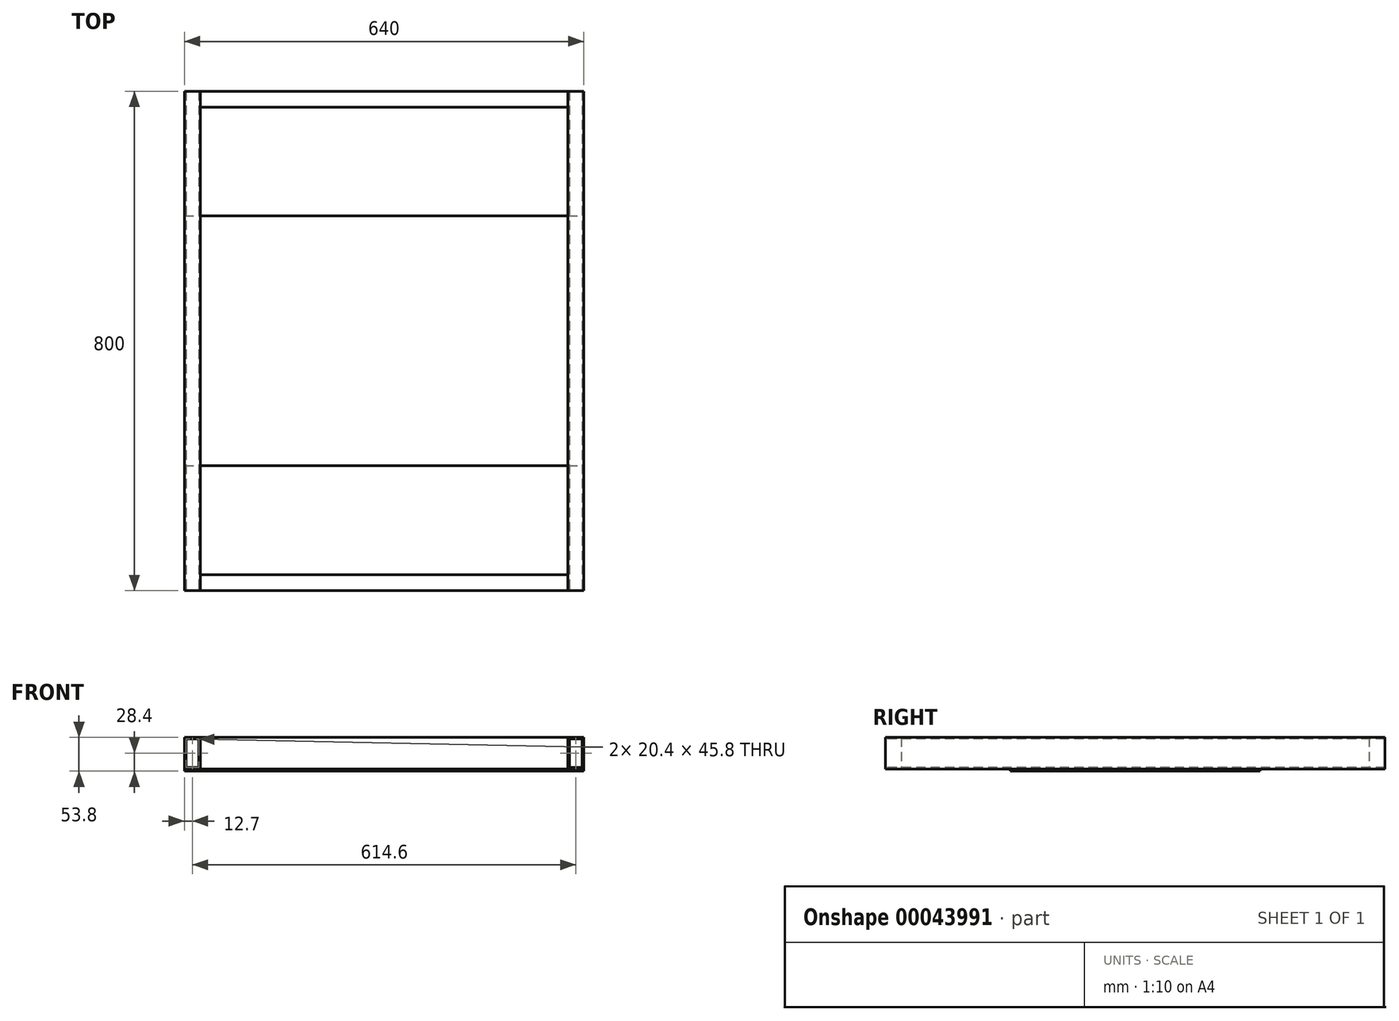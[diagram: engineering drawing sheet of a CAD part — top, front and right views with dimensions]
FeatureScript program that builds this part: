
annotation { "Feature Type Name" : "Feature", "Feature Type Description" : "" }
export const myFeature = defineFeature(function(context is Context, id is Id, definition is map)
    precondition{}
    {
        {
            var Q0;
            Q0=qCreatedBy(makeId("Top.planeOp"),FACE);
            var sketch = newSketch(context, id + "F0", { "sketchPlane" : qUnion([Q0])});
            skLineSegment(sketch, "E0", {"start": v(0, 0) * mm, "end": v(294.6, 0) * mm, "construction": true});
            skLineSegment(sketch, "E1", {"start": v(0, 0) * mm, "end": v(-294.6, 0) * mm, "construction": true});
            skLineSegment(sketch, "E2.bottom", {"start": v(-320, 400) * mm, "end": v(-294.6, 400) * mm});
            skLineSegment(sketch, "E2.top", {"start": v(-320, -400) * mm, "end": v(-294.6, -400) * mm});
            skLineSegment(sketch, "E2.left", {"start": v(-320, 400) * mm, "end": v(-320, -400) * mm});
            skLineSegment(sketch, "E2.right", {"start": v(-294.6, 400) * mm, "end": v(-294.6, -400) * mm});
            skLineSegment(sketch, "E3.bottom", {"start": v(294.6, 400) * mm, "end": v(320, 400) * mm});
            skLineSegment(sketch, "E3.top", {"start": v(294.6, -400) * mm, "end": v(320, -400) * mm});
            skLineSegment(sketch, "E3.left", {"start": v(294.6, 400) * mm, "end": v(294.6, -400) * mm});
            skLineSegment(sketch, "E3.right", {"start": v(320, 400) * mm, "end": v(320, -400) * mm});
            skLineSegment(sketch, "E4.bottom", {"start": v(-294.6, 400) * mm, "end": v(294.6, 400) * mm});
            skLineSegment(sketch, "E4.top", {"start": v(-294.6, 374.6) * mm, "end": v(294.6, 374.6) * mm});
            skLineSegment(sketch, "E4.left", {"start": v(-294.6, 400) * mm, "end": v(-294.6, 374.6) * mm});
            skLineSegment(sketch, "E4.right", {"start": v(294.6, 400) * mm, "end": v(294.6, 374.6) * mm});
            skLineSegment(sketch, "E5.bottom", {"start": v(-294.6, -400) * mm, "end": v(294.6, -400) * mm});
            skLineSegment(sketch, "E5.top", {"start": v(-294.6, -374.6) * mm, "end": v(294.6, -374.6) * mm});
            skLineSegment(sketch, "E5.left", {"start": v(-294.6, -400) * mm, "end": v(-294.6, -374.6) * mm});
            skLineSegment(sketch, "E5.right", {"start": v(294.6, -400) * mm, "end": v(294.6, -374.6) * mm});
            skSolve(sketch);
        }
        {
            var Q0;
            Q0=makeQuery(id+"F0.imprint","IMPRINT",FACE,{"disambiguationData":[TD([[makeQuery(id+"F0.imprint","IMPRINT",EDGE,{"derivedFrom":sQuery(id+"F0.wireOp",EDGE,"E2.bottom")}),-1.0]])]});
            extrude(context, id + "F1", {"entities" : qUnion([Q0]), "depth" : 50.8 * mm});
        }
        {
            var Q0;
            Q0=makeQuery(id+"F0.imprint","IMPRINT",FACE,{"disambiguationData":[TD([[makeQuery(id+"F0.imprint","IMPRINT",EDGE,{"derivedFrom":sQuery(id+"F0.wireOp",EDGE,"E4.bottom")}),-1.0]])]});
            extrude(context, id + "F2", {"entities" : qUnion([Q0]), "depth" : 50.8 * mm});
        }
        {
            var Q0;
            Q0=makeQuery(id+"F0.imprint","IMPRINT",FACE,{"disambiguationData":[TD([[makeQuery(id+"F0.imprint","IMPRINT",EDGE,{"derivedFrom":sQuery(id+"F0.wireOp",EDGE,"E3.bottom")}),-1.0]])]});
            extrude(context, id + "F3", {"entities" : qUnion([Q0]), "depth" : 50.8 * mm});
        }
        {
            var Q0;
            Q0=makeQuery(id+"F0.imprint","IMPRINT",FACE,{"disambiguationData":[TD([[makeQuery(id+"F0.imprint","IMPRINT",EDGE,{"derivedFrom":sQuery(id+"F0.wireOp",EDGE,"E5.bottom")}),1.0]])]});
            extrude(context, id + "F4", {"entities" : qUnion([Q0]), "depth" : 50.8 * mm});
        }
        {
            var Q0;
            Q0=makeQuery(id+"F0.imprint","IMPRINT",FACE,{"disambiguationData":[TD([[makeQuery(id+"F0.imprint","IMPRINT",EDGE,{"derivedFrom":sQuery(id+"F0.wireOp",EDGE,"E2.right")}),1.0]])]});
            var sketch = newSketch(context, id + "F5", { "sketchPlane" : qUnion([Q0])});
            skLineSegment(sketch, "E6.rect.bottom", {"start": v(-320, -200) * mm, "end": v(320, -200) * mm});
            skLineSegment(sketch, "E6.rect.top", {"start": v(-320, 200) * mm, "end": v(320, 200) * mm});
            skLineSegment(sketch, "E6.rect.left", {"start": v(-320, -200) * mm, "end": v(-320, 200) * mm});
            skLineSegment(sketch, "E6.rect.right", {"start": v(320, -200) * mm, "end": v(320, 200) * mm});
            skPoint(sketch, "E6.rect.middle", {"position": v(0, 0) * mm});
            skSolve(sketch);
        }
        {
            var Q0;
            Q0 = qSketchRegion(id + "F5", true);
            extrude(context, id + "F6", {"entities" : qUnion([Q0]), "oppositeDirection" : true, "depth" : 3 * mm});
        }
        {
            var Q0;
            Q0=makeQuery(id+"F1.opExtrude","SWEPT_FACE",FACE,{"disambiguationData":[OSD([sQuery(id+"F0.wireOp",EDGE,"E2.top")])]});
            var Q1;
            Q1=makeQuery(id+"F3.opExtrude","SWEPT_FACE",FACE,{"disambiguationData":[OSD([sQuery(id+"F0.wireOp",EDGE,"E3.top")])]});
            var Q2;
            Q2=makeQuery(id+"F1.opExtrude","SWEPT_FACE",FACE,{"disambiguationData":[OSD([sQuery(id+"F0.wireOp",EDGE,"E2.bottom")])]});
            var Q3;
            Q3=makeQuery(id+"F3.opExtrude","SWEPT_FACE",FACE,{"disambiguationData":[OSD([sQuery(id+"F0.wireOp",EDGE,"E3.bottom")])]});
            var Q4;
            Q4=makeQuery(id+"F2.opExtrude","SWEPT_FACE",FACE,{"disambiguationData":[OSD([sQuery(id+"F0.wireOp",EDGE,"E4.right")])]});
            var Q5;
            Q5=makeQuery(id+"F2.opExtrude","SWEPT_FACE",FACE,{"disambiguationData":[OSD([sQuery(id+"F0.wireOp",EDGE,"E4.left")])]});
            var Q6;
            Q6=makeQuery(id+"F4.opExtrude","SWEPT_FACE",FACE,{"disambiguationData":[OSD([sQuery(id+"F0.wireOp",EDGE,"E5.left")])]});
            var Q7;
            Q7=makeQuery(id+"F4.opExtrude","SWEPT_FACE",FACE,{"disambiguationData":[OSD([sQuery(id+"F0.wireOp",EDGE,"E5.right")])]});
            shell(context, id + "F7", {"entities" : qUnion([Q0, Q1, Q2, Q3, Q4, Q5, Q6, Q7]), "thickness" : 2.5 * mm});
        }
    });
